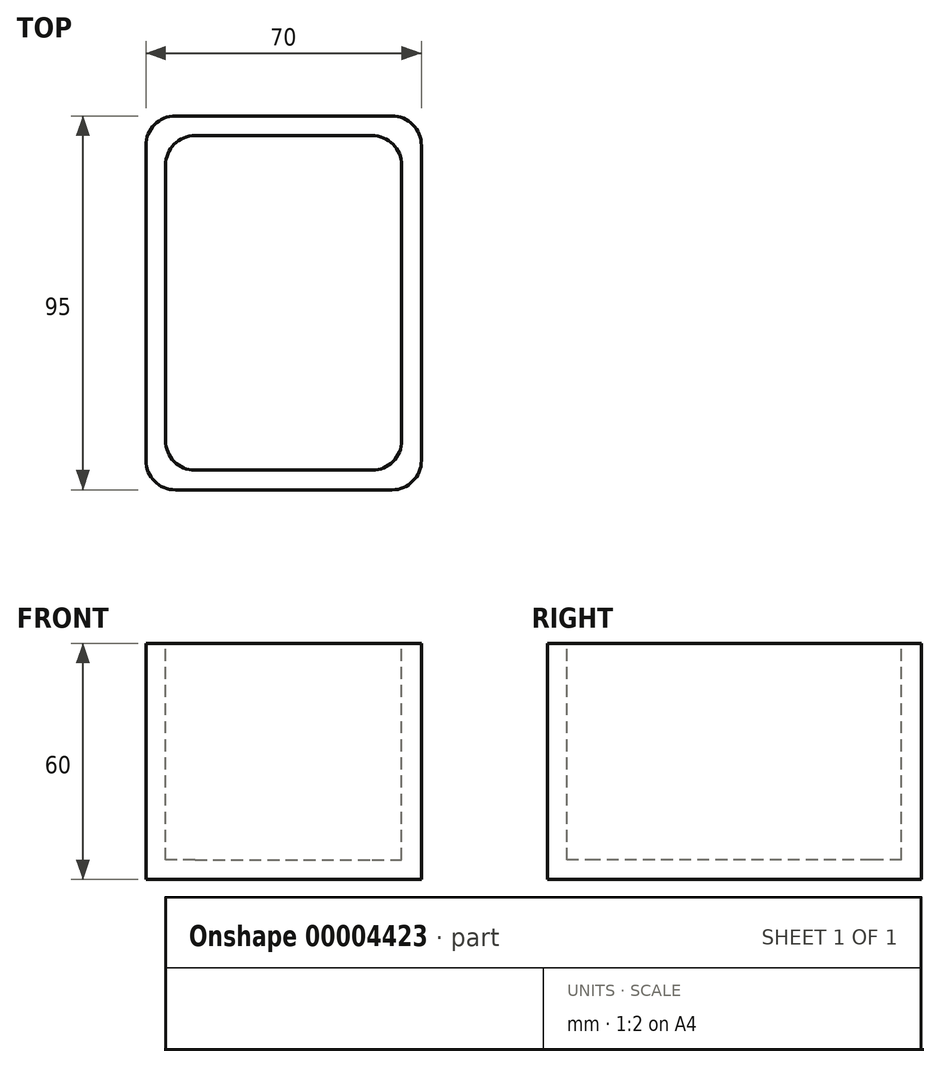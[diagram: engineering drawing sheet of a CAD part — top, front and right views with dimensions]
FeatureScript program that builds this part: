
annotation { "Feature Type Name" : "Feature", "Feature Type Description" : "" }
export const myFeature = defineFeature(function(context is Context, id is Id, definition is map)
    precondition{}
    {
        {
            var Q0;
            Q0=qCreatedBy(makeId("Top.planeOp"),FACE);
            var sketch = newSketch(context, id + "F0", { "sketchPlane" : qUnion([Q0])});
            skLineSegment(sketch, "E0.bottom", {"start": v(7.5, 0) * mm, "end": v(62.5, 0) * mm});
            skLineSegment(sketch, "E0.top", {"start": v(7.5, 95) * mm, "end": v(62.5, 95) * mm});
            skLineSegment(sketch, "E0.left", {"start": v(0, 7.5) * mm, "end": v(0, 87.5) * mm});
            skLineSegment(sketch, "E0.right", {"start": v(70, 7.5) * mm, "end": v(70, 87.5) * mm});
            skPoint(sketch, "E1.visualSharp", {"position": v(0, 0) * mm});
            skArc(sketch, "E1.filletArc", {"start": v(0, 7.5) * mm, "mid": v(2.2, 2.2) * mm, "end": v(7.5, 0) * mm});
            skPoint(sketch, "E2.visualSharp", {"position": v(0, 95) * mm});
            skArc(sketch, "E2.filletArc", {"start": v(7.5, 95) * mm, "mid": v(2.2, 92.8) * mm, "end": v(0, 87.5) * mm});
            skPoint(sketch, "E3.visualSharp", {"position": v(70, 95) * mm});
            skArc(sketch, "E3.filletArc", {"start": v(70, 87.5) * mm, "mid": v(67.8, 92.8) * mm, "end": v(62.5, 95) * mm});
            skPoint(sketch, "E4.visualSharp", {"position": v(70, 0) * mm});
            skArc(sketch, "E4.filletArc", {"start": v(62.5, 0) * mm, "mid": v(67.8, 2.2) * mm, "end": v(70, 7.5) * mm});
            skSolve(sketch);
        }
        {
            var Q0;
            Q0=makeQuery(id+"F0.imprint","IMPRINT",FACE,{"disambiguationData":[TD([[makeQuery(id+"F0.imprint","IMPRINT",EDGE,{"derivedFrom":sQuery(id+"F0.wireOp",EDGE,"E0.bottom")}),1.0]])]});
            extrude(context, id + "F1", {"entities" : qUnion([Q0]), "depth" : 60 * mm});
        }
        {
            var Q0;
            Q0=makeQuery(id+"F1.opExtrude","CAP_FACE",FACE,{"disambiguationData":[OSD([sQuery(id+"F0.wireOp",EDGE,"E0.bottom"),sQuery(id+"F0.wireOp",EDGE,"E0.top"),sQuery(id+"F0.wireOp",EDGE,"E0.left"),sQuery(id+"F0.wireOp",EDGE,"E0.right"),sQuery(id+"F0.wireOp",EDGE,"E1.filletArc"),sQuery(id+"F0.wireOp",EDGE,"E2.filletArc"),sQuery(id+"F0.wireOp",EDGE,"E3.filletArc"),sQuery(id+"F0.wireOp",EDGE,"E4.filletArc")])],"isStart":false});
            var sketch = newSketch(context, id + "F2", { "sketchPlane" : qUnion([Q0])});
            skLineSegment(sketch, "E5.bottom", {"start": v(12.5, 90) * mm, "end": v(57.5, 90) * mm});
            skLineSegment(sketch, "E5.top", {"start": v(12.5, 5) * mm, "end": v(57.5, 5) * mm});
            skLineSegment(sketch, "E5.left", {"start": v(5, 82.5) * mm, "end": v(5, 12.5) * mm});
            skLineSegment(sketch, "E5.right", {"start": v(65, 82.5) * mm, "end": v(65, 12.5) * mm});
            skPoint(sketch, "E6.visualSharp", {"position": v(5, 5) * mm});
            skArc(sketch, "E6.filletArc", {"start": v(5, 12.5) * mm, "mid": v(7.2, 7.2) * mm, "end": v(12.5, 5) * mm});
            skPoint(sketch, "E7.visualSharp", {"position": v(5, 90) * mm});
            skArc(sketch, "E7.filletArc", {"start": v(12.5, 90) * mm, "mid": v(7.2, 87.8) * mm, "end": v(5, 82.5) * mm});
            skPoint(sketch, "E8.visualSharp", {"position": v(65, 90) * mm});
            skArc(sketch, "E8.filletArc", {"start": v(65, 82.5) * mm, "mid": v(62.8, 87.8) * mm, "end": v(57.5, 90) * mm});
            skPoint(sketch, "E9.visualSharp", {"position": v(65, 5) * mm});
            skArc(sketch, "E9.filletArc", {"start": v(57.5, 5) * mm, "mid": v(62.8, 7.2) * mm, "end": v(65, 12.5) * mm});
            skSolve(sketch);
        }
        {
            var Q0;
            Q0=makeQuery(id+"F2.imprint","IMPRINT",FACE,{"disambiguationData":[TD([[makeQuery(id+"F2.imprint","IMPRINT",EDGE,{"derivedFrom":sQuery(id+"F2.wireOp",EDGE,"E5.bottom")}),-1.0]])]});
            extrude(context, id + "F3", {"entities" : qUnion([Q0]), "operationType" : NewBodyOperationType.REMOVE, "oppositeDirection" : true, "depth" : 55 * mm});
        }
    });
